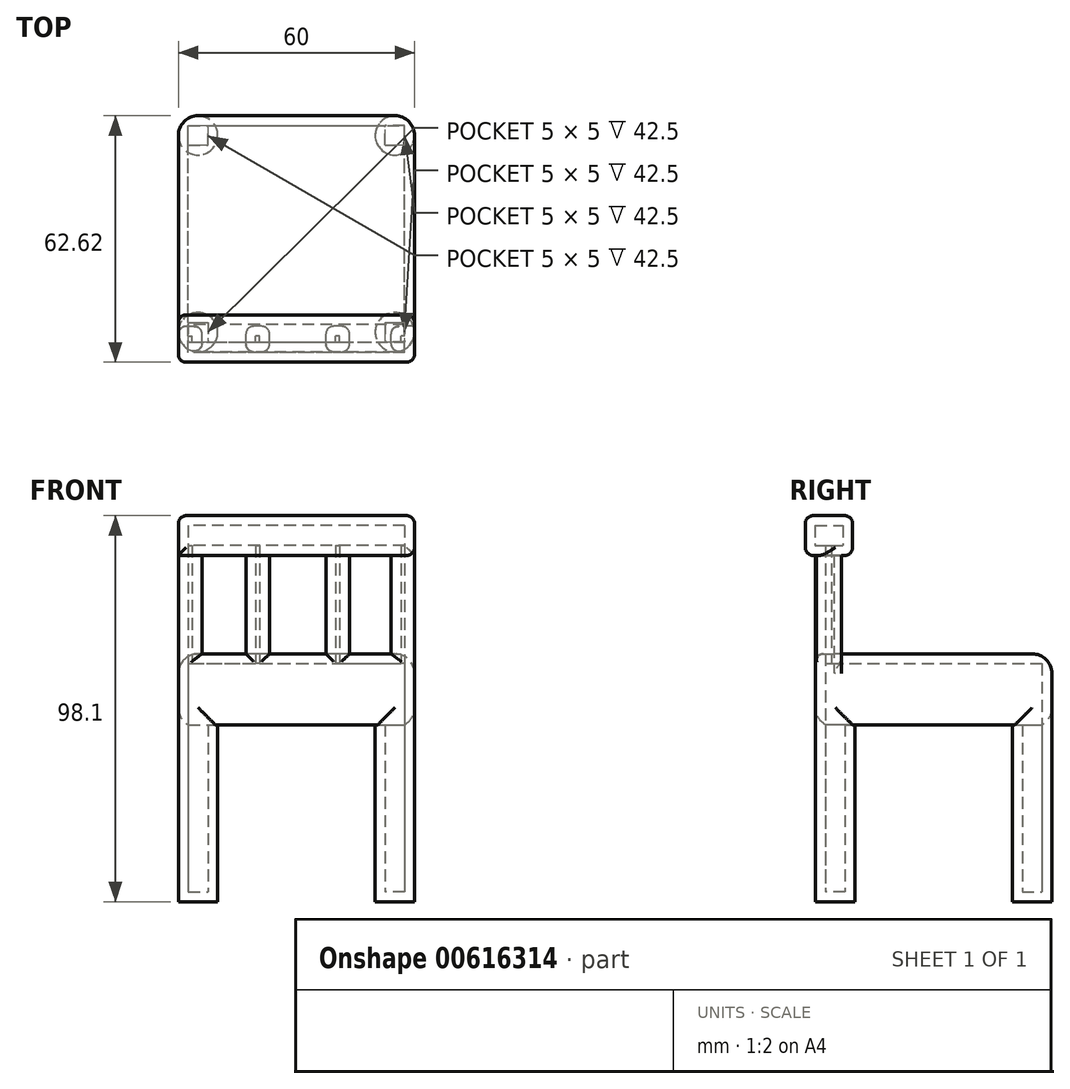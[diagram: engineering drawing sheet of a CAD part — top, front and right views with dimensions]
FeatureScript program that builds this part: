
annotation { "Feature Type Name" : "Feature", "Feature Type Description" : "" }
export const myFeature = defineFeature(function(context is Context, id is Id, definition is map)
    precondition{}
    {
        {
            var Q0;
            Q0=qCreatedBy(makeId("Top.planeOp"),FACE);
            var sketch = newSketch(context, id + "F0", { "sketchPlane" : qUnion([Q0])});
            skLineSegment(sketch, "E0.bottom", {"start": v(-30, -30) * mm, "end": v(30, -30) * mm});
            skLineSegment(sketch, "E0.top", {"start": v(-30, 30) * mm, "end": v(30, 30) * mm});
            skLineSegment(sketch, "E0.left", {"start": v(-30, -30) * mm, "end": v(-30, 30) * mm});
            skLineSegment(sketch, "E0.right", {"start": v(30, -30) * mm, "end": v(30, 30) * mm});
            skPoint(sketch, "E0.middle", {"position": v(0, 0) * mm});
            skSolve(sketch);
        }
        {
            var Q0;
            Q0 = qSketchRegion(id + "F0", true);
            extrude(context, id + "F1", {"entities" : qUnion([Q0]), "depth" : 18 * mm, "offsetDistance" : 25 * mm});
        }
        {
            var Q0;
            Q0=makeQuery(id+"F1.opExtrude","SWEPT_FACE",FACE,{"disambiguationData":[OSD([sQuery(id+"F0.wireOp",EDGE,"E0.bottom")])]});
            var sketch = newSketch(context, id + "F2", { "sketchPlane" : qUnion([Q0])});
            skLineSegment(sketch, "E1.bottom", {"start": v(-30, 0) * mm, "end": v(-20, 0) * mm});
            skLineSegment(sketch, "E1.top", {"start": v(-30, -45) * mm, "end": v(-20, -45) * mm});
            skLineSegment(sketch, "E1.left", {"start": v(-30, 0) * mm, "end": v(-30, -45) * mm});
            skLineSegment(sketch, "E1.right", {"start": v(-20, 0) * mm, "end": v(-20, -45) * mm});
            skLineSegment(sketch, "E2.bottom", {"start": v(30, 0) * mm, "end": v(20, 0) * mm});
            skLineSegment(sketch, "E2.top", {"start": v(30, -45) * mm, "end": v(20, -45) * mm});
            skLineSegment(sketch, "E2.left", {"start": v(30, 0) * mm, "end": v(30, -45) * mm});
            skLineSegment(sketch, "E2.right", {"start": v(20, 0) * mm, "end": v(20, -45) * mm});
            skLineSegment(sketch, "E3.bottom", {"start": v(-20, 0) * mm, "end": v(-30, 0) * mm});
            skLineSegment(sketch, "E3.top", {"start": v(-20, -45) * mm, "end": v(-30, -45) * mm});
            skSolve(sketch);
        }
        {
            var Q0;
            Q0 = qSketchRegion(id + "F2", true);
            extrude(context, id + "F3", {"entities" : qUnion([Q0]), "operationType" : NewBodyOperationType.ADD, "oppositeDirection" : true, "depth" : 10 * mm, "offsetDistance" : 25 * mm});
        }
        {
            var Q0;
            Q0=makeQuery(id+"F1.opExtrude","SWEPT_FACE",FACE,{"disambiguationData":[OSD([sQuery(id+"F0.wireOp",EDGE,"E0.top")])]});
            var sketch = newSketch(context, id + "F4", { "sketchPlane" : qUnion([Q0])});
            skLineSegment(sketch, "E4.bottom", {"start": v(-30, 0) * mm, "end": v(-20, 0) * mm});
            skLineSegment(sketch, "E4.top", {"start": v(-30, -45) * mm, "end": v(-20, -45) * mm});
            skLineSegment(sketch, "E4.left", {"start": v(-30, 0) * mm, "end": v(-30, -45) * mm});
            skLineSegment(sketch, "E4.right", {"start": v(-20, 0) * mm, "end": v(-20, -45) * mm});
            skLineSegment(sketch, "E5.bottom", {"start": v(30, 0) * mm, "end": v(20, 0) * mm});
            skLineSegment(sketch, "E5.top", {"start": v(30, -45) * mm, "end": v(20, -45) * mm});
            skLineSegment(sketch, "E5.left", {"start": v(30, 0) * mm, "end": v(30, -45) * mm});
            skLineSegment(sketch, "E5.right", {"start": v(20, 0) * mm, "end": v(20, -45) * mm});
            skSolve(sketch);
        }
        {
            var Q0;
            Q0 = qSketchRegion(id + "F4", true);
            extrude(context, id + "F5", {"entities" : qUnion([Q0]), "operationType" : NewBodyOperationType.ADD, "oppositeDirection" : true, "depth" : 10 * mm, "offsetDistance" : 25 * mm});
        }
        {
            var Q0;
            Q0=makeQuery(id+"F1.opExtrude","CAP_FACE",FACE,{"disambiguationData":[OSD([sQuery(id+"F0.wireOp",EDGE,"E0.bottom"),sQuery(id+"F0.wireOp",EDGE,"E0.top"),sQuery(id+"F0.wireOp",EDGE,"E0.left"),sQuery(id+"F0.wireOp",EDGE,"E0.right")])],"isStart":false});
            var sketch = newSketch(context, id + "F6", { "sketchPlane" : qUnion([Q0])});
            skLineSegment(sketch, "E6.bottom", {"start": v(30, -30) * mm, "end": v(24, -30) * mm});
            skLineSegment(sketch, "E6.top", {"start": v(30, -23.5) * mm, "end": v(24, -23.5) * mm});
            skLineSegment(sketch, "E6.left", {"start": v(30, -30) * mm, "end": v(30, -23.5) * mm});
            skLineSegment(sketch, "E6.right", {"start": v(24, -30) * mm, "end": v(24, -23.5) * mm});
            skLineSegment(sketch, "E7.bottom", {"start": v(13.48, -30) * mm, "end": v(7.48, -30) * mm});
            skLineSegment(sketch, "E7.top", {"start": v(13.48, -23.5) * mm, "end": v(7.48, -23.5) * mm});
            skLineSegment(sketch, "E7.left", {"start": v(13.48, -30) * mm, "end": v(13.48, -23.5) * mm});
            skLineSegment(sketch, "E7.right", {"start": v(7.48, -30) * mm, "end": v(7.48, -23.5) * mm});
            skLineSegment(sketch, "E8.bottom", {"start": v(-6.84, -30) * mm, "end": v(-12.84, -30) * mm});
            skLineSegment(sketch, "E8.top", {"start": v(-6.84, -23.5) * mm, "end": v(-12.84, -23.5) * mm});
            skLineSegment(sketch, "E8.left", {"start": v(-6.84, -30) * mm, "end": v(-6.84, -23.5) * mm});
            skLineSegment(sketch, "E8.right", {"start": v(-12.84, -30) * mm, "end": v(-12.84, -23.5) * mm});
            skLineSegment(sketch, "E9.bottom", {"start": v(-30, -30) * mm, "end": v(-24, -30) * mm});
            skLineSegment(sketch, "E9.top", {"start": v(-30, -23.5) * mm, "end": v(-24, -23.5) * mm});
            skLineSegment(sketch, "E9.left", {"start": v(-30, -30) * mm, "end": v(-30, -23.5) * mm});
            skLineSegment(sketch, "E9.right", {"start": v(-24, -30) * mm, "end": v(-24, -23.5) * mm});
            skSolve(sketch);
        }
        {
            var Q0;
            Q0 = qSketchRegion(id + "F6", true);
            extrude(context, id + "F7", {"entities" : qUnion([Q0]), "operationType" : NewBodyOperationType.ADD, "depth" : 25 * mm, "offsetDistance" : 25 * mm});
        }
        {
            var Q0;
            Q0=makeQuery(id+"F7.opExtrude","CAP_FACE",FACE,{"disambiguationData":[OSD([sQuery(id+"F6.wireOp",EDGE,"E6.bottom"),sQuery(id+"F6.wireOp",EDGE,"E6.top"),sQuery(id+"F6.wireOp",EDGE,"E6.left"),sQuery(id+"F6.wireOp",EDGE,"E6.right")])],"isStart":false});
            var sketch = newSketch(context, id + "F8", { "sketchPlane" : qUnion([Q0])});
            skPoint(sketch, "E10.firstSnap0", {"position": v(30, -26.75) * mm});
            skLineSegment(sketch, "E10.bottom", {"start": v(30, -32.62) * mm, "end": v(-30, -32.62) * mm});
            skLineSegment(sketch, "E10.top", {"start": v(30, -20.62) * mm, "end": v(-30, -20.62) * mm});
            skLineSegment(sketch, "E10.left", {"start": v(30, -32.62) * mm, "end": v(30, -20.62) * mm});
            skLineSegment(sketch, "E10.right", {"start": v(-30, -32.62) * mm, "end": v(-30, -20.62) * mm});
            skSolve(sketch);
        }
        {
            var Q0;
            Q0 = qSketchRegion(id + "F8", true);
            extrude(context, id + "F9", {"entities" : qUnion([Q0]), "operationType" : NewBodyOperationType.ADD, "depth" : 10.1 * mm, "offsetDistance" : 25 * mm});
        }
        {
            var Q0;
            Q0=makeQuery(id+"F1.opExtrude","CAP_FACE",FACE,{"disambiguationData":[OSD([sQuery(id+"F0.wireOp",EDGE,"E0.bottom"),sQuery(id+"F0.wireOp",EDGE,"E0.top"),sQuery(id+"F0.wireOp",EDGE,"E0.left"),sQuery(id+"F0.wireOp",EDGE,"E0.right")])],"isStart":true});
            shell(context, id + "F10", {"entities" : qUnion([Q0]), "thickness" : 2.5 * mm});
        }
        {
            var Q0;
            Q0=makeQuery(id+"F5.opExtrude","CAP_EDGE",EDGE,{"disambiguationData":[OSD([sQuery(id+"F4.wireOp",EDGE,"E5.right")])],"isStart":true});
            var Q1;
            Q1=makeQuery(id+"F5.opExtrude","CAP_EDGE",EDGE,{"disambiguationData":[OSD([sQuery(id+"F4.wireOp",EDGE,"E5.right")])],"isStart":false});
            var Q2;
            Q2=makeQuery(id+"F5.boolean.opBoolean","MERGE",EDGE,{"derivedFrom":[makeQuery(id+"F1.opExtrude","SWEPT_EDGE",EDGE,{"disambiguationData":[OSD([sQuery(id+"F0.wireOp",EDGE,"E0.top"),sQuery(id+"F0.wireOp",EDGE,"E0.left")])]}),makeQuery(id+"F5.opExtrude","CAP_EDGE",EDGE,{"disambiguationData":[OSD([sQuery(id+"F4.wireOp",EDGE,"E5.left")])],"isStart":true})]});
            var Q3;
            Q3=makeQuery(id+"F5.opExtrude","CAP_EDGE",EDGE,{"disambiguationData":[OSD([sQuery(id+"F4.wireOp",EDGE,"E5.left")])],"isStart":false});
            var Q4;
            Q4=makeQuery(id+"F5.boolean.opBoolean","MERGE",EDGE,{"derivedFrom":[makeQuery(id+"F1.opExtrude","SWEPT_EDGE",EDGE,{"disambiguationData":[OSD([sQuery(id+"F0.wireOp",EDGE,"E0.top"),sQuery(id+"F0.wireOp",EDGE,"E0.right")])]}),makeQuery(id+"F5.opExtrude","CAP_EDGE",EDGE,{"disambiguationData":[OSD([sQuery(id+"F4.wireOp",EDGE,"E4.left")])],"isStart":true})]});
            var Q5;
            Q5=makeQuery(id+"F5.opExtrude","CAP_EDGE",EDGE,{"disambiguationData":[OSD([sQuery(id+"F4.wireOp",EDGE,"E4.left")])],"isStart":false});
            var Q6;
            Q6=makeQuery(id+"F5.opExtrude","CAP_EDGE",EDGE,{"disambiguationData":[OSD([sQuery(id+"F4.wireOp",EDGE,"E4.right")])],"isStart":true});
            var Q7;
            Q7=makeQuery(id+"F5.opExtrude","CAP_EDGE",EDGE,{"disambiguationData":[OSD([sQuery(id+"F4.wireOp",EDGE,"E4.right")])],"isStart":false});
            var Q8;
            Q8=makeQuery(id+"F3.opExtrude","CAP_EDGE",EDGE,{"disambiguationData":[OSD([sQuery(id+"F2.wireOp",EDGE,"E1.left")])],"isStart":false});
            var Q9;
            Q9=makeQuery(id+"F7.boolean.opBoolean","MERGE",EDGE,{"derivedFrom":[makeQuery(id+"F3.boolean.opBoolean","MERGE",EDGE,{"derivedFrom":[makeQuery(id+"F1.opExtrude","SWEPT_EDGE",EDGE,{"disambiguationData":[OSD([sQuery(id+"F0.wireOp",EDGE,"E0.bottom"),sQuery(id+"F0.wireOp",EDGE,"E0.left")])]}),makeQuery(id+"F3.opExtrude","CAP_EDGE",EDGE,{"disambiguationData":[OSD([sQuery(id+"F2.wireOp",EDGE,"E1.left")])],"isStart":true})]}),makeQuery(id+"F7.opExtrude","SWEPT_EDGE",EDGE,{"disambiguationData":[OSD([sQuery(id+"F6.wireOp",EDGE,"E9.bottom"),sQuery(id+"F6.wireOp",EDGE,"E9.left")])]})]});
            var Q10;
            Q10=makeQuery(id+"F3.opExtrude","CAP_EDGE",EDGE,{"disambiguationData":[OSD([sQuery(id+"F2.wireOp",EDGE,"E1.right")])],"isStart":true});
            var Q11;
            Q11=makeQuery(id+"F3.opExtrude","CAP_EDGE",EDGE,{"disambiguationData":[OSD([sQuery(id+"F2.wireOp",EDGE,"E1.right")])],"isStart":false});
            var Q12;
            Q12=makeQuery(id+"F3.opExtrude","CAP_EDGE",EDGE,{"disambiguationData":[OSD([sQuery(id+"F2.wireOp",EDGE,"E2.right")])],"isStart":true});
            var Q13;
            Q13=makeQuery(id+"F7.boolean.opBoolean","MERGE",EDGE,{"derivedFrom":[makeQuery(id+"F3.boolean.opBoolean","MERGE",EDGE,{"derivedFrom":[makeQuery(id+"F1.opExtrude","SWEPT_EDGE",EDGE,{"disambiguationData":[OSD([sQuery(id+"F0.wireOp",EDGE,"E0.bottom"),sQuery(id+"F0.wireOp",EDGE,"E0.right")])]}),makeQuery(id+"F3.opExtrude","CAP_EDGE",EDGE,{"disambiguationData":[OSD([sQuery(id+"F2.wireOp",EDGE,"E2.left")])],"isStart":true})]}),makeQuery(id+"F7.opExtrude","SWEPT_EDGE",EDGE,{"disambiguationData":[OSD([sQuery(id+"F6.wireOp",EDGE,"E6.bottom"),sQuery(id+"F6.wireOp",EDGE,"E6.left")])]})]});
            var Q14;
            Q14=makeQuery(id+"F3.opExtrude","CAP_EDGE",EDGE,{"disambiguationData":[OSD([sQuery(id+"F2.wireOp",EDGE,"E2.left")])],"isStart":false});
            var Q15;
            Q15=makeQuery(id+"F3.opExtrude","CAP_EDGE",EDGE,{"disambiguationData":[OSD([sQuery(id+"F2.wireOp",EDGE,"E2.right")])],"isStart":false});
            fillet(context, id + "F11", {"entities" : qUnion([Q0, Q1, Q2, Q3, Q4, Q5, Q6, Q7, Q8, Q9, Q10, Q11, Q12, Q13, Q14, Q15]), "radius" : 5 * mm, "tangentPropagation" : true, "allowEdgeOverflow" : false});
        }
        {
            var Q0;
            Q0=makeQuery(id+"F1.opExtrude","CAP_EDGE",EDGE,{"disambiguationData":[OSD([sQuery(id+"F0.wireOp",EDGE,"E0.top")])],"isStart":false});
            var Q1;
            Q1=makeQuery(id+"F1.opExtrude","CAP_EDGE",EDGE,{"disambiguationData":[OSD([sQuery(id+"F0.wireOp",EDGE,"E0.right")])],"isStart":true});
            var Q2;
            Q2=makeQuery(id+"F1.opExtrude","CAP_EDGE",EDGE,{"disambiguationData":[OSD([sQuery(id+"F0.wireOp",EDGE,"E0.bottom")])],"isStart":true});
            var Q3;
            Q3=makeQuery(id+"F1.opExtrude","CAP_EDGE",EDGE,{"disambiguationData":[OSD([sQuery(id+"F0.wireOp",EDGE,"E0.left")])],"isStart":true});
            var Q4;
            Q4=makeQuery(id+"F1.opExtrude","CAP_EDGE",EDGE,{"disambiguationData":[OSD([sQuery(id+"F0.wireOp",EDGE,"E0.top")])],"isStart":true});
            fillet(context, id + "F12", {"entities" : qUnion([Q0, Q1, Q2, Q3, Q4]), "radius" : 5 * mm, "tangentPropagation" : true, "allowEdgeOverflow" : false});
        }
        {
            var Q0;
            Q0=makeQuery(id+"F7.opExtrude","SWEPT_EDGE",EDGE,{"disambiguationData":[OSD([sQuery(id+"F6.wireOp",EDGE,"E7.top"),sQuery(id+"F6.wireOp",EDGE,"E7.right")])]});
            var Q1;
            Q1=makeQuery(id+"F7.opExtrude","SWEPT_EDGE",EDGE,{"disambiguationData":[OSD([sQuery(id+"F0.wireOp",EDGE,"E0.bottom"),sQuery(id+"F6.wireOp",EDGE,"E7.bottom"),sQuery(id+"F6.wireOp",EDGE,"E7.right")])]});
            var Q2;
            Q2=makeQuery(id+"F7.opExtrude","SWEPT_EDGE",EDGE,{"disambiguationData":[OSD([sQuery(id+"F6.wireOp",EDGE,"E8.top"),sQuery(id+"F6.wireOp",EDGE,"E8.right")])]});
            var Q3;
            Q3=makeQuery(id+"F7.opExtrude","SWEPT_EDGE",EDGE,{"disambiguationData":[OSD([sQuery(id+"F0.wireOp",EDGE,"E0.bottom"),sQuery(id+"F6.wireOp",EDGE,"E8.bottom"),sQuery(id+"F6.wireOp",EDGE,"E8.right")])]});
            var Q4;
            Q4=makeQuery(id+"F7.opExtrude","SWEPT_EDGE",EDGE,{"disambiguationData":[OSD([sQuery(id+"F0.wireOp",EDGE,"E0.bottom"),sQuery(id+"F6.wireOp",EDGE,"E9.bottom"),sQuery(id+"F6.wireOp",EDGE,"E9.right")])]});
            var Q5;
            Q5=makeQuery(id+"F7.opExtrude","SWEPT_EDGE",EDGE,{"disambiguationData":[OSD([sQuery(id+"F0.wireOp",EDGE,"E0.bottom"),sQuery(id+"F6.wireOp",EDGE,"E8.bottom"),sQuery(id+"F6.wireOp",EDGE,"E8.left")])]});
            var Q6;
            Q6=makeQuery(id+"F7.opExtrude","SWEPT_EDGE",EDGE,{"disambiguationData":[OSD([sQuery(id+"F6.wireOp",EDGE,"E8.top"),sQuery(id+"F6.wireOp",EDGE,"E8.left")])]});
            var Q7;
            Q7=makeQuery(id+"F7.opExtrude","SWEPT_EDGE",EDGE,{"disambiguationData":[OSD([sQuery(id+"F6.wireOp",EDGE,"E6.top"),sQuery(id+"F6.wireOp",EDGE,"E6.right")])]});
            var Q8;
            Q8=makeQuery(id+"F7.opExtrude","SWEPT_EDGE",EDGE,{"disambiguationData":[OSD([sQuery(id+"F0.wireOp",EDGE,"E0.bottom"),sQuery(id+"F6.wireOp",EDGE,"E7.bottom"),sQuery(id+"F6.wireOp",EDGE,"E7.left")])]});
            var Q9;
            Q9=makeQuery(id+"F9.opExtrude","SWEPT_EDGE",EDGE,{"disambiguationData":[OSD([sQuery(id+"F8.wireOp",EDGE,"E10.top"),sQuery(id+"F8.wireOp",EDGE,"E10.left")])]});
            var Q10;
            {var subQ0=sQuery(id+"F8.wireOp",EDGE,"E10.left");Q10=makeQuery(id+"F9.boolean.opBoolean","SPLIT",EDGE,{"disambiguationData":[TD([makeQuery(id+"F1.opExtrude","SWEPT_FACE",FACE,{"disambiguationData":[OSD([sQuery(id+"F0.wireOp",EDGE,"E0.bottom")])]})])],"derivedFrom":makeQuery(id+"F9.opExtrude","CAP_EDGE",EDGE,{"disambiguationData":[OSD([subQ0])],"isStart":true})});}
            var Q11;
            Q11=makeQuery(id+"F9.opExtrude","SWEPT_EDGE",EDGE,{"disambiguationData":[OSD([sQuery(id+"F8.wireOp",EDGE,"E10.bottom"),sQuery(id+"F8.wireOp",EDGE,"E10.left")])]});
            var Q12;
            Q12=makeQuery(id+"F9.opExtrude","CAP_EDGE",EDGE,{"disambiguationData":[OSD([sQuery(id+"F8.wireOp",EDGE,"E10.left")])],"isStart":false});
            var Q13;
            Q13=makeQuery(id+"F9.opExtrude","CAP_EDGE",EDGE,{"disambiguationData":[OSD([sQuery(id+"F8.wireOp",EDGE,"E10.right")])],"isStart":false});
            var Q14;
            Q14=makeQuery(id+"F9.opExtrude","SWEPT_EDGE",EDGE,{"disambiguationData":[OSD([sQuery(id+"F8.wireOp",EDGE,"E10.top"),sQuery(id+"F8.wireOp",EDGE,"E10.right")])]});
            var Q15;
            Q15=makeQuery(id+"F9.opExtrude","CAP_EDGE",EDGE,{"disambiguationData":[OSD([sQuery(id+"F8.wireOp",EDGE,"E10.bottom")])],"isStart":true});
            var Q16;
            Q16=makeQuery(id+"F9.opExtrude","SWEPT_EDGE",EDGE,{"disambiguationData":[OSD([sQuery(id+"F8.wireOp",EDGE,"E10.bottom"),sQuery(id+"F8.wireOp",EDGE,"E10.right")])]});
            var Q17;
            Q17=makeQuery(id+"F9.opExtrude","CAP_EDGE",EDGE,{"disambiguationData":[OSD([sQuery(id+"F8.wireOp",EDGE,"E10.bottom")])],"isStart":false});
            var Q18;
            Q18=makeQuery(id+"F9.opExtrude","CAP_FACE",FACE,{"disambiguationData":[OSD([sQuery(id+"F8.wireOp",EDGE,"E10.bottom"),sQuery(id+"F8.wireOp",EDGE,"E10.top"),sQuery(id+"F8.wireOp",EDGE,"E10.left"),sQuery(id+"F8.wireOp",EDGE,"E10.right")])],"isStart":false});
            var Q19;
            Q19=makeQuery(id+"F9.opExtrude","CAP_EDGE",EDGE,{"disambiguationData":[OSD([sQuery(id+"F8.wireOp",EDGE,"E10.top")])],"isStart":true});
            var Q20;
            {var subQ0=sQuery(id+"F0.wireOp",EDGE,"E0.bottom");Q20=makeQuery(id+"F7.boolean.opBoolean","SPLIT",EDGE,{"disambiguationData":[TD([makeQuery(id+"F7.opExtrude","SWEPT_FACE",FACE,{"disambiguationData":[OSD([sQuery(id+"F6.wireOp",EDGE,"E6.right")])]})])],"derivedFrom":makeQuery(id+"F1.opExtrude","CAP_EDGE",EDGE,{"disambiguationData":[OSD([subQ0])],"isStart":false})});}
            var Q21;
            {var subQ0=sQuery(id+"F0.wireOp",EDGE,"E0.bottom");Q21=makeQuery(id+"F7.boolean.opBoolean","SPLIT",EDGE,{"disambiguationData":[TD([makeQuery(id+"F7.opExtrude","SWEPT_FACE",FACE,{"disambiguationData":[OSD([sQuery(id+"F6.wireOp",EDGE,"E7.right")])]})])],"derivedFrom":makeQuery(id+"F1.opExtrude","CAP_EDGE",EDGE,{"disambiguationData":[OSD([subQ0])],"isStart":false})});}
            var Q22;
            {var subQ0=sQuery(id+"F0.wireOp",EDGE,"E0.bottom");Q22=makeQuery(id+"F7.boolean.opBoolean","SPLIT",EDGE,{"disambiguationData":[TD([makeQuery(id+"F7.opExtrude","SWEPT_FACE",FACE,{"disambiguationData":[OSD([sQuery(id+"F6.wireOp",EDGE,"E8.right")])]})])],"derivedFrom":makeQuery(id+"F1.opExtrude","CAP_EDGE",EDGE,{"disambiguationData":[OSD([subQ0])],"isStart":false})});}
            var Q23;
            Q23=makeQuery(id+"F7.opExtrude","SWEPT_EDGE",EDGE,{"disambiguationData":[OSD([sQuery(id+"F6.wireOp",EDGE,"E9.top"),sQuery(id+"F6.wireOp",EDGE,"E9.right")])]});
            var Q24;
            Q24=makeQuery(id+"F7.opExtrude","SWEPT_EDGE",EDGE,{"disambiguationData":[OSD([sQuery(id+"F0.wireOp",EDGE,"E0.left"),sQuery(id+"F6.wireOp",EDGE,"E9.top"),sQuery(id+"F6.wireOp",EDGE,"E9.left")])]});
            var Q25;
            Q25=makeQuery(id+"F7.opExtrude","SWEPT_EDGE",EDGE,{"disambiguationData":[OSD([sQuery(id+"F6.wireOp",EDGE,"E7.top"),sQuery(id+"F6.wireOp",EDGE,"E7.left")])]});
            var Q26;
            Q26=makeQuery(id+"F7.opExtrude","SWEPT_EDGE",EDGE,{"disambiguationData":[OSD([sQuery(id+"F0.wireOp",EDGE,"E0.bottom"),sQuery(id+"F6.wireOp",EDGE,"E6.bottom"),sQuery(id+"F6.wireOp",EDGE,"E6.right")])]});
            fillet(context, id + "F13", {"entities" : qUnion([Q0, Q1, Q2, Q3, Q4, Q5, Q6, Q7, Q8, Q9, Q10, Q11, Q12, Q13, Q14, Q15, Q16, Q17, Q18, Q19, Q20, Q21, Q22, Q23, Q24, Q25, Q26]), "radius" : 2 * mm, "tangentPropagation" : true, "allowEdgeOverflow" : false});
        }
    });
